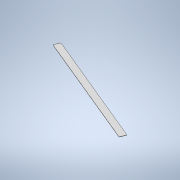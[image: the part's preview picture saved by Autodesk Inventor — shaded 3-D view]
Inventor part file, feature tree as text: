
AUTODESK INVENTOR PART (.ipt)
format: ipt  version: 2022 (Build 260153000, 153)  size: 96,768 bytes
history: native  units: mm
features: extrude x1, sketch x1
ambient origin geometry x8: Origin, YZ Plane, XZ Plane, XY Plane, X Axis, Y Axis, Z Axis, Center Point
bodies: Solid1 (feature_tree)
feature tree (2):
  extrude  "Extrusion1"  TaperAngle=22.5deg  [1 undecoded]
  sketch  "Sketch1"  dims[d2=1000.0mm d3=22.5deg d4=50.0mm d5=2.0mm d6=0.0mm]
note: 1 required parameter value undecoded (feature->parameter linkage not recoverable at this tier; creation-order binding heuristic only, values carry confidence <= 0.55)
